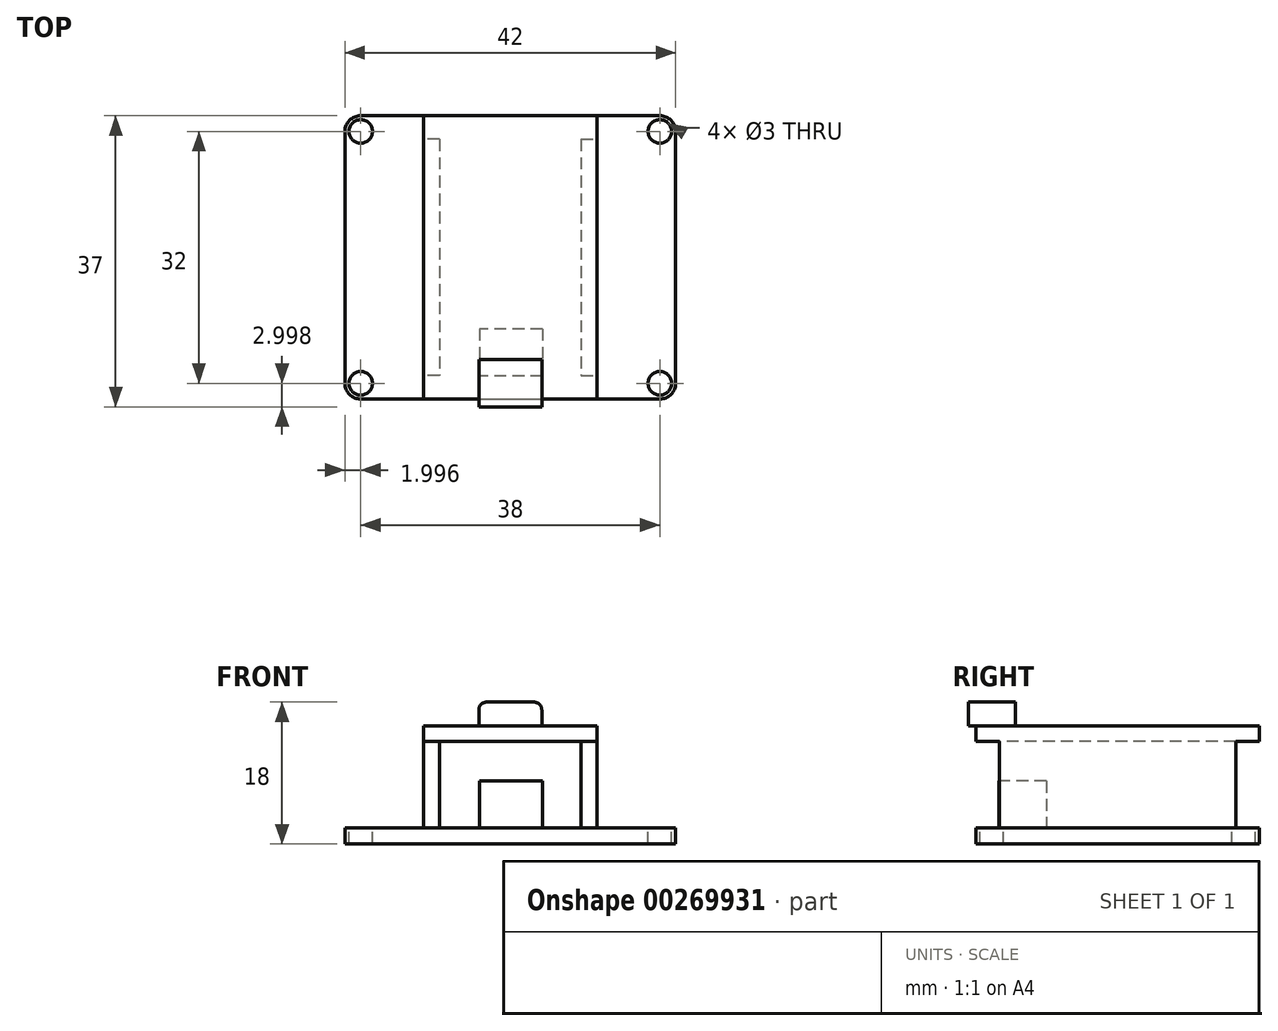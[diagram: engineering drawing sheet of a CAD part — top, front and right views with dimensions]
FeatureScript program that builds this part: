
annotation { "Feature Type Name" : "Feature", "Feature Type Description" : "" }
export const myFeature = defineFeature(function(context is Context, id is Id, definition is map)
    precondition{}
    {
        {
            var Q0;
            Q0=qCreatedBy(makeId("Top.planeOp"),FACE);
            var sketch = newSketch(context, id + "F0", { "sketchPlane" : qUnion([Q0])});
            skLineSegment(sketch, "E0.bottom", {"start": v(-14.25, 12.56) * mm, "end": v(27.75, 12.56) * mm});
            skLineSegment(sketch, "E0.top", {"start": v(-14.25, -23.44) * mm, "end": v(27.75, -23.44) * mm});
            skLineSegment(sketch, "E0.left", {"start": v(-14.25, 12.56) * mm, "end": v(-14.25, -23.44) * mm});
            skLineSegment(sketch, "E0.right", {"start": v(27.75, 12.56) * mm, "end": v(27.75, -23.44) * mm});
            skSolve(sketch);
        }
        {
            var Q0;
            Q0=makeQuery(id+"F0.imprint","IMPRINT",FACE,{"disambiguationData":[TD([[makeQuery(id+"F0.imprint","IMPRINT",EDGE,{"derivedFrom":sQuery(id+"F0.wireOp",EDGE,"E0.bottom")}),-1.0]])]});
            extrude(context, id + "F1", {"entities" : qUnion([Q0]), "depth" : 2 * mm});
        }
        {
            var Q0;
            Q0=makeQuery(id+"F1.opExtrude","SWEPT_EDGE",EDGE,{"disambiguationData":[OSD([sQuery(id+"F0.wireOp",EDGE,"E0.top"),sQuery(id+"F0.wireOp",EDGE,"E0.right")])]});
            var Q1;
            Q1=makeQuery(id+"F1.opExtrude","SWEPT_EDGE",EDGE,{"disambiguationData":[OSD([sQuery(id+"F0.wireOp",EDGE,"E0.bottom"),sQuery(id+"F0.wireOp",EDGE,"E0.right")])]});
            var Q2;
            Q2=makeQuery(id+"F1.opExtrude","SWEPT_EDGE",EDGE,{"disambiguationData":[OSD([sQuery(id+"F0.wireOp",EDGE,"E0.top"),sQuery(id+"F0.wireOp",EDGE,"E0.left")])]});
            var Q3;
            Q3=makeQuery(id+"F1.opExtrude","SWEPT_EDGE",EDGE,{"disambiguationData":[OSD([sQuery(id+"F0.wireOp",EDGE,"E0.bottom"),sQuery(id+"F0.wireOp",EDGE,"E0.left")])]});
            fillet(context, id + "F2", {"entities" : qUnion([Q0, Q1, Q2, Q3]), "radius" : 2 * mm, "tangentPropagation" : true, "allowEdgeOverflow" : false});
        }
        {
            var Q0;
            Q0=makeQuery(id+"F1.opExtrude","CAP_FACE",FACE,{"disambiguationData":[OSD([sQuery(id+"F0.wireOp",EDGE,"E0.bottom"),sQuery(id+"F0.wireOp",EDGE,"E0.top"),sQuery(id+"F0.wireOp",EDGE,"E0.left"),sQuery(id+"F0.wireOp",EDGE,"E0.right")])],"isStart":false});
            var sketch = newSketch(context, id + "F3", { "sketchPlane" : qUnion([Q0])});
            skCircle(sketch, "E1", {"center": v(25.75, 10.56) * mm, "radius": 1.5 * mm});
            skCircle(sketch, "E2", {"center": v(-12.25, 10.56) * mm, "radius": 1.5 * mm});
            skCircle(sketch, "E3", {"center": v(-12.25, -21.44) * mm, "radius": 1.5 * mm});
            skCircle(sketch, "E4", {"center": v(25.75, -21.44) * mm, "radius": 1.5 * mm});
            skSolve(sketch);
        }
        {
            var Q0;
            Q0=makeQuery(id+"F3.imprint","IMPRINT",FACE,{"disambiguationData":[TD([[makeQuery(id+"F3.imprint","IMPRINT",EDGE,{"derivedFrom":sQuery(id+"F3.wireOp",EDGE,"E2")}),1.0]])]});
            var Q1;
            Q1=makeQuery(id+"F3.imprint","IMPRINT",FACE,{"disambiguationData":[TD([[makeQuery(id+"F3.imprint","IMPRINT",EDGE,{"derivedFrom":sQuery(id+"F3.wireOp",EDGE,"E3")}),1.0]])]});
            var Q2;
            Q2=makeQuery(id+"F3.imprint","IMPRINT",FACE,{"disambiguationData":[TD([[makeQuery(id+"F3.imprint","IMPRINT",EDGE,{"derivedFrom":sQuery(id+"F3.wireOp",EDGE,"E4")}),1.0]])]});
            var Q3;
            Q3=makeQuery(id+"F3.imprint","IMPRINT",FACE,{"disambiguationData":[TD([[makeQuery(id+"F3.imprint","IMPRINT",EDGE,{"derivedFrom":sQuery(id+"F3.wireOp",EDGE,"E1")}),1.0]])]});
            extrude(context, id + "F4", {"entities" : qUnion([Q0, Q1, Q2, Q3]), "operationType" : NewBodyOperationType.REMOVE, "oppositeDirection" : true, "depth" : 2 * mm});
        }
        {
            var Q0;
            Q0=makeQuery(id+"F1.opExtrude","CAP_FACE",FACE,{"disambiguationData":[OSD([sQuery(id+"F0.wireOp",EDGE,"E0.bottom"),sQuery(id+"F0.wireOp",EDGE,"E0.top"),sQuery(id+"F0.wireOp",EDGE,"E0.left"),sQuery(id+"F0.wireOp",EDGE,"E0.right")])],"isStart":true});
            var sketch = newSketch(context, id + "F5", { "sketchPlane" : qUnion([Q0])});
            skLineSegment(sketch, "E5", {"start": v(-22.63, 5.44) * mm, "end": v(40.2, 5.44) * mm, "construction": true});
            skPoint(sketch, "E5.startSnap0", {"position": v(-14.25, 5.44) * mm});
            skPoint(sketch, "E6.middle", {"position": v(-4.25, 5.44) * mm});
            skLineSegment(sketch, "E7", {"start": v(6.75, -17.67) * mm, "end": v(6.75, 26.9) * mm, "construction": true});
            skPoint(sketch, "E7.startSnap0", {"position": v(6.75, -12.56) * mm});
            skPoint(sketch, "E7.endSnap0", {"position": v(6.75, 23.44) * mm});
            skLineSegment(sketch, "E8.MirrorCS", {"start": v(15.75, 20.44) * mm, "end": v(17.75, 20.44) * mm});
            skLineSegment(sketch, "E9.MirrorCS", {"start": v(15.75, -9.56) * mm, "end": v(15.75, 20.44) * mm});
            skLineSegment(sketch, "E10.MirrorCS", {"start": v(15.75, -9.56) * mm, "end": v(17.75, -9.56) * mm});
            skLineSegment(sketch, "E11.MirrorCS", {"start": v(17.75, -9.56) * mm, "end": v(17.75, 20.44) * mm});
            skLineSegment(sketch, "E12.MirrorCS", {"start": v(-2.25, 20.44) * mm, "end": v(-4.25, 20.44) * mm});
            skLineSegment(sketch, "E13.MirrorCS", {"start": v(-4.25, -9.56) * mm, "end": v(-4.25, 20.44) * mm});
            skLineSegment(sketch, "E14.MirrorCS", {"start": v(-2.25, -9.56) * mm, "end": v(-2.25, 20.44) * mm});
            skLineSegment(sketch, "E15.MirrorCS", {"start": v(-2.25, -9.56) * mm, "end": v(-4.25, -9.56) * mm});
            skSolve(sketch);
        }
        {
            var Q0;
            Q0=makeQuery(id+"F1.opExtrude","CAP_FACE",FACE,{"disambiguationData":[OSD([sQuery(id+"F0.wireOp",EDGE,"E0.bottom"),sQuery(id+"F0.wireOp",EDGE,"E0.top"),sQuery(id+"F0.wireOp",EDGE,"E0.left"),sQuery(id+"F0.wireOp",EDGE,"E0.right")])],"isStart":false});
            var sketch = newSketch(context, id + "F6", { "sketchPlane" : qUnion([Q0])});
            skLineSegment(sketch, "E16.4", {"start": v(15.75, 9.56) * mm, "end": v(17.75, 9.56) * mm});
            skLineSegment(sketch, "E16.5", {"start": v(15.75, 9.56) * mm, "end": v(15.75, -20.44) * mm});
            skLineSegment(sketch, "E16.6", {"start": v(17.75, 9.56) * mm, "end": v(17.75, -20.44) * mm});
            skLineSegment(sketch, "E16.7", {"start": v(15.75, -20.44) * mm, "end": v(17.75, -20.44) * mm});
            skLineSegment(sketch, "E17.MirrorCS", {"start": v(-2.25, 9.56) * mm, "end": v(-4.25, 9.56) * mm});
            skLineSegment(sketch, "E18.MirrorCS", {"start": v(-2.25, 9.56) * mm, "end": v(-2.25, -20.44) * mm});
            skLineSegment(sketch, "E19.MirrorCS", {"start": v(-4.25, 9.56) * mm, "end": v(-4.25, -20.44) * mm});
            skLineSegment(sketch, "E20.MirrorCS", {"start": v(-2.25, -20.44) * mm, "end": v(-4.25, -20.44) * mm});
            skLineSegment(sketch, "E21.bottom", {"start": v(10.83, -14.51) * mm, "end": v(2.83, -14.51) * mm});
            skLineSegment(sketch, "E21.top", {"start": v(10.83, -20.51) * mm, "end": v(2.83, -20.51) * mm});
            skLineSegment(sketch, "E21.left", {"start": v(10.83, -14.51) * mm, "end": v(10.83, -20.51) * mm});
            skLineSegment(sketch, "E21.right", {"start": v(2.83, -14.51) * mm, "end": v(2.83, -20.51) * mm});
            skPoint(sketch, "E21.middle", {"position": v(4.43, -19.51) * mm});
            skSolve(sketch);
        }
        {
            var Q0;
            Q0=makeQuery(id+"F6.imprint","IMPRINT",FACE,{"disambiguationData":[TD([[makeQuery(id+"F6.imprint","IMPRINT",EDGE,{"derivedFrom":sQuery(id+"F6.wireOp",EDGE,"E16.0")}),1.0]])]});
            var Q1;
            Q1=makeQuery(id+"F6.imprint","IMPRINT",FACE,{"disambiguationData":[TD([[makeQuery(id+"F6.imprint","IMPRINT",EDGE,{"derivedFrom":sQuery(id+"F6.wireOp",EDGE,"E16.4")}),-1.0]])]});
            var Q2;
            Q2=makeQuery(id+"F6.imprint","IMPRINT",FACE,{"disambiguationData":[TD([[makeQuery(id+"F6.imprint","IMPRINT",EDGE,{"derivedFrom":sQuery(id+"F6.wireOp",EDGE,"E17.MirrorCS")}),1.0]])]});
            extrude(context, id + "F7", {"entities" : qUnion([Q0, Q1, Q2]), "operationType" : NewBodyOperationType.ADD, "depth" : 11 * mm});
        }
        {
            var Q0;
            Q0=makeQuery(id+"F7.opExtrude","CAP_FACE",FACE,{"disambiguationData":[OSD([sQuery(id+"F6.wireOp",EDGE,"E17.MirrorCS"),sQuery(id+"F6.wireOp",EDGE,"E18.MirrorCS"),sQuery(id+"F6.wireOp",EDGE,"E19.MirrorCS"),sQuery(id+"F6.wireOp",EDGE,"E20.MirrorCS")])],"isStart":false});
            var sketch = newSketch(context, id + "F8", { "sketchPlane" : qUnion([Q0])});
            skLineSegment(sketch, "E22.bottom", {"start": v(-4.25, 12.56) * mm, "end": v(17.75, 12.56) * mm});
            skLineSegment(sketch, "E22.top", {"start": v(-4.25, -23.44) * mm, "end": v(17.75, -23.44) * mm});
            skLineSegment(sketch, "E22.left", {"start": v(-4.25, 12.56) * mm, "end": v(-4.25, -23.44) * mm});
            skLineSegment(sketch, "E22.right", {"start": v(17.75, 12.56) * mm, "end": v(17.75, -23.44) * mm});
            skSolve(sketch);
        }
        {
            var Q0;
            Q0=qSketchRegion(id+"F8",true);
            extrude(context, id + "F9", {"entities" : qUnion([Q0]), "operationType" : NewBodyOperationType.ADD, "depth" : 2 * mm});
        }
        {
            var Q0;
            Q0=makeQuery(id+"F9.opExtrude","CAP_FACE",FACE,{"disambiguationData":[OSD([sQuery(id+"F8.wireOp",EDGE,"E22.bottom"),sQuery(id+"F8.wireOp",EDGE,"E22.top"),sQuery(id+"F8.wireOp",EDGE,"E22.left"),sQuery(id+"F8.wireOp",EDGE,"E22.right")])],"isStart":false});
            var sketch = newSketch(context, id + "F10", { "sketchPlane" : qUnion([Q0])});
            skLineSegment(sketch, "E23.bottom", {"start": v(10.75, -24.44) * mm, "end": v(2.75, -24.44) * mm});
            skLineSegment(sketch, "E23.top", {"start": v(10.75, -18.44) * mm, "end": v(2.75, -18.44) * mm});
            skLineSegment(sketch, "E23.left", {"start": v(10.75, -24.44) * mm, "end": v(10.75, -18.44) * mm});
            skLineSegment(sketch, "E23.right", {"start": v(2.75, -24.44) * mm, "end": v(2.75, -18.44) * mm});
            skPoint(sketch, "E23.middle", {"position": v(6.75, -23.44) * mm});
            skSolve(sketch);
        }
        {
            var Q0;
            {var subQ0=sQuery(id+"F10.wireOp",EDGE,"E23.top");Q0=makeQuery(id+"F10.imprint","IMPRINT",FACE,{"disambiguationData":[TD([[makeQuery(id+"F10.imprint","IMPRINT",EDGE,{"derivedFrom":subQ0}),1.0]])]});}
            var Q1;
            {var subQ0=sQuery(id+"F10.wireOp",EDGE,"E23.bottom");Q1=makeQuery(id+"F10.imprint","IMPRINT",FACE,{"disambiguationData":[TD([[makeQuery(id+"F10.imprint","IMPRINT",EDGE,{"derivedFrom":subQ0}),-1.0]])]});}
            extrude(context, id + "F11", {"entities" : qUnion([Q0, Q1]), "operationType" : NewBodyOperationType.ADD, "depth" : 3 * mm});
        }
        {
            var Q0;
            Q0=makeQuery(id+"F11.opExtrude","CAP_EDGE",EDGE,{"disambiguationData":[OSD([sQuery(id+"F10.wireOp",EDGE,"E23.left")])],"isStart":false});
            var Q1;
            Q1=makeQuery(id+"F11.opExtrude","CAP_EDGE",EDGE,{"disambiguationData":[OSD([sQuery(id+"F10.wireOp",EDGE,"E23.right")])],"isStart":false});
            fillet(context, id + "F12", {"entities" : qUnion([Q0, Q1]), "radius" : 1 * mm, "tangentPropagation" : true, "allowEdgeOverflow" : false});
        }
        {
            var Q0;
            Q0=makeQuery(id+"F6.imprint","IMPRINT",FACE,{"disambiguationData":[TD([[makeQuery(id+"F6.imprint","IMPRINT",EDGE,{"derivedFrom":sQuery(id+"F6.wireOp",EDGE,"E21.bottom")}),1.0]])]});
            extrude(context, id + "F13", {"entities" : qUnion([Q0]), "operationType" : NewBodyOperationType.ADD, "depth" : 6 * mm});
        }
        {
            var Q0;
            Q0=makeQuery(id+"F1.opExtrude","SWEPT_BODY",BODY,{"disambiguationData":[OSD([sQuery(id+"F0.wireOp",EDGE,"E0.bottom"),sQuery(id+"F0.wireOp",EDGE,"E0.top"),sQuery(id+"F0.wireOp",EDGE,"E0.left"),sQuery(id+"F0.wireOp",EDGE,"E0.right")])]});
            transform(context, id + "F14", {"entities" : qUnion([Q0]), "transformType" : TransformType.TRANSLATION_3D, "dx" : 0 * mm, "dy" : 0 * mm, "dz" : 0 * mm, "makeCopy" : true});
        }
        {
            var Q0;
            Q0=makeQuery(id+"F14.opPattern","COPY",BODY,{"derivedFrom":makeQuery(id+"F1.opExtrude","SWEPT_BODY",BODY,{"disambiguationData":[OSD([sQuery(id+"F0.wireOp",EDGE,"E0.bottom"),sQuery(id+"F0.wireOp",EDGE,"E0.top"),sQuery(id+"F0.wireOp",EDGE,"E0.left"),sQuery(id+"F0.wireOp",EDGE,"E0.right")])]}),"instanceName":"1"});
            deleteBodies(context, id + "F15", {"entities" : qUnion([Q0])});
        }
    });
